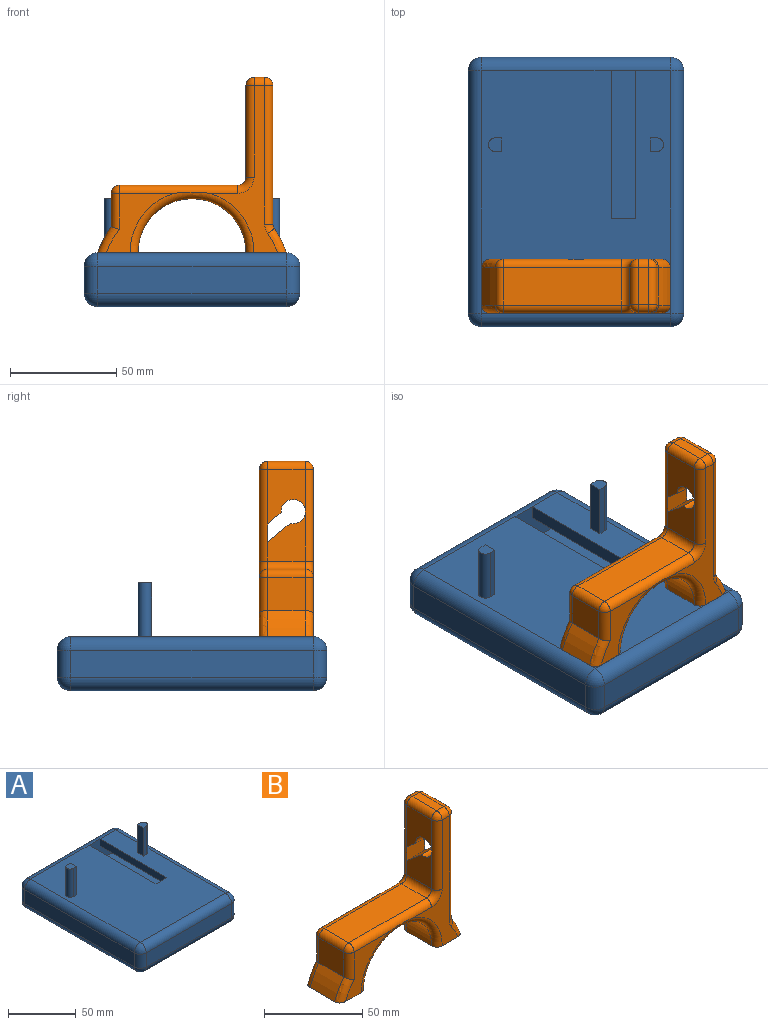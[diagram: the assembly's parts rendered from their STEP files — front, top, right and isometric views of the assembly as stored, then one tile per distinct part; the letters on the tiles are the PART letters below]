
ASSEMBLY  parts=2 mates=1
PART A: 45 faces, bbox 101.6x127x50.8 mm
  f0: plane 114.3x88.9mm, normal (0,0,1), area 9290.9mm2, adj f9,f10,f19,f20,f26,f27,f28,f29
  f1: plane 114.3x12.7mm, normal (-1,0,0), area 1451.6mm2, adj f14,f19,f22,f25
  f2: plane 88.9x12.7mm, normal (0,-1,0), area 1129mm2, adj f11,f20,f21,f25
  f3: plane 114.3x12.7mm, normal (1,0,0), area 1451.6mm2, adj f6,f10,f11,f12
  f4: plane 88.9x12.7mm, normal (0,1,0), area 1129mm2, adj f6,f9,f13,f14
  f5: plane 114.3x88.9mm, normal (0,0,-1), area 10161.3mm2, adj f12,f13,f21,f22
  f6: cylinder r=6.35mm len=12.7mm, axis (0,0,1), area 126.7mm2, adj f3,f4,f7,f8
  f7: sphere r=6.35mm, area 63.3mm2, adj f6,f9,f10
  f8: sphere r=6.35mm, area 63.3mm2, adj f6,f12,f13
  f9: cylinder r=6.35mm len=88.9mm, axis (1,0,0), area 886.7mm2, adj f0,f4,f7,f15,f42
  f10: cylinder r=6.35mm len=114.3mm, axis (0,-1,0), area 1140.1mm2, adj f0,f3,f7,f16
  f11: cylinder r=6.35mm len=12.7mm, axis (0,0,-1), area 126.7mm2, adj f2,f3,f16,f17
  f12: cylinder r=6.35mm len=114.3mm, axis (0,1,0), area 1140.1mm2, adj f3,f5,f8,f17
  f13: cylinder r=6.35mm len=88.9mm, axis (-1,0,0), area 886.7mm2, adj f4,f5,f8,f18
  f14: cylinder r=6.35mm len=12.7mm, axis (0,0,-1), area 126.7mm2, adj f1,f4,f15,f18
  f15: sphere r=6.35mm, area 63.3mm2, adj f9,f14,f19
  f16: sphere r=6.35mm, area 63.3mm2, adj f10,f11,f20
  f17: sphere r=6.35mm, area 63.3mm2, adj f11,f12,f21
  f18: sphere r=6.35mm, area 63.3mm2, adj f13,f14,f22
  f19: cylinder r=6.35mm len=114.3mm, axis (0,1,0), area 1140.1mm2, adj f0,f1,f15,f23
  f20: cylinder r=6.35mm len=88.9mm, axis (-1,0,0), area 886.7mm2, adj f0,f2,f16,f23
  f21: cylinder r=6.35mm len=88.9mm, axis (1,0,0), area 886.7mm2, adj f2,f5,f17,f24
  f22: cylinder r=6.35mm len=114.3mm, axis (0,-1,0), area 1140.1mm2, adj f1,f5,f18,f24
  f23: sphere r=6.35mm, area 63.3mm2, adj f19,f20,f25
  f24: sphere r=6.35mm, area 63.3mm2, adj f21,f22,f25
  f25: cylinder r=6.35mm len=12.7mm, axis (0,0,1), area 126.7mm2, adj f1,f2,f23,f24
  f26: plane 25.4x3.18mm, normal (0,-1,0), area 80.6mm2, adj f0,f27,f29,f30
  f27: plane 25.4x6.35mm, normal (1,0,0), area 161.3mm2, adj f0,f26,f28,f30
  f28: plane 25.4x3.18mm, normal (0,1,0), area 80.6mm2, adj f0,f27,f29,f30
  f29: cylinder r=3.17mm len=25.4mm, axis (0,0,-1), area 253.4mm2, adj f0,f26,f28,f30
  f30: plane 6.35x6.35mm, normal (0,0,1), area 36mm2, adj f26,f27,f28,f29
  f31: plane 25.4x6.35mm, normal (-1,0,0), area 161.3mm2, adj f0,f32,f34,f35
  f32: plane 25.4x3.18mm, normal (0,-1,0), area 80.6mm2, adj f0,f31,f33,f35
  f33: cylinder r=3.17mm len=25.4mm, axis (0,0,-1), area 253.4mm2, adj f0,f32,f34,f35
  f34: plane 25.4x3.18mm, normal (0,1,0), area 80.6mm2, adj f0,f31,f33,f35
  f35: plane 6.35x6.35mm, normal (0,0,1), area 36mm2, adj f31,f32,f33,f34
  f36: plane 11.43x6.35mm, normal (0,1,0), area 72.6mm2, adj f0,f37,f38,f43
  f37: plane 69.85x6.35mm, normal (-1,0,0), area 443.5mm2, adj f0,f36,f42,f43
  f38: plane 69.85x6.35mm, normal (1,0,0), area 443.5mm2, adj f0,f36,f42,f43
  f39: plane 114.3x12.7mm, normal (1,0,0), area 1451.6mm2, adj f40,f42,f43,f44
  f40: plane 88.9x12.7mm, normal (0,1,0), area 1129mm2, adj f39,f41,f43,f44
  f41: plane 114.3x12.7mm, normal (-1,0,0), area 1451.6mm2, adj f40,f42,f43,f44
  f42: plane 88.9x19.05mm, normal (0,-1,0), area 1201.6mm2, adj f9,f37,f38,f39,f41,f43,f44
  f43: plane 114.3x88.9mm, normal (0,0,-1), area 9362.9mm2, adj f36,f37,f38,f39,f40,f41,f42
  f44: plane 114.3x88.9mm, normal (0,0,1), area 10161.3mm2, adj f39,f40,f41,f42
PART B: 53 faces, bbox 89.9x25.4x84.7 mm
  f0: plane 25.67x17.78mm, normal (1,0,0), area 321.6mm2, adj f19,f29,f30,f51,f52
  f1: plane 25.67x17.78mm, normal (-1,0,0), area 321.6mm2, adj f34,f40,f46,f51,f52
  f2: plane 31.88x27.94mm, normal (0,1,0), area 332.7mm2, adj f6,f18,f22,f27,f33
  f3: plane 31.88x27.94mm, normal (0,-1,0), area 332.7mm2, adj f6,f25,f31,f37,f42
  f4: plane 17.78x15.68mm, normal (-1,0,0), area 278.7mm2, adj f5,f22,f31,f32
  f5: cylinder r=46.99mm len=17.78mm, axis (0,1,0), area 246.4mm2, adj f4,f6,f18,f25
  f6: plane 25.4x19.05mm, normal (0,0,-1), area 471mm2, adj f2,f3,f5,f7,f18,f25,f27,f37
  f7: cylinder r=25.4mm len=50.8mm, axis (0,1,0), area 1418.8mm2, adj f6,f8,f27,f37
  f8: plane 25.4x19.05mm, normal (0,0,-1), area 471mm2, adj f7,f9,f14,f15,f16,f21,f27,f37
  f9: cylinder r=46.99mm len=17.78mm, axis (0,1,0), area 225.8mm2, adj f8,f16,f20,f21
  f10: plane 44.96x17.78mm, normal (1,0,0), area 667.7mm2, adj f19,f20,f30,f48,f49
  f11: plane 17.78x5.08mm, normal (0,0,1), area 90.3mm2, adj f28,f29,f40,f41
  f12: plane 22.87x17.78mm, normal (-1,0,0), area 274.9mm2, adj f34,f43,f46,f48,f49
  f13: plane 55.88x17.78mm, normal (0,0,1), area 993.5mm2, adj f32,f33,f42,f43
  f14: plane 78.74x31.88mm, normal (0,-1,0), area 603.8mm2, adj f8,f21,f24,f30,f37,f41,f42,f45
  f15: plane 78.74x31.88mm, normal (0,1,0), area 603.8mm2, adj f8,f16,f17,f19,f27,f28,f33,f34
  f16: torus R=43.18mm, axis (0,-1,0), area 70.9mm2, adj f8,f9,f15,f17
  f17: torus R=7.62mm, axis (0,-1,0), area 18.7mm2, adj f15,f16,f19,f20
  f18: torus R=43.18mm, axis (0,-1,0), area 80.3mm2, adj f2,f5,f6,f22
  f19: cylinder r=3.81mm len=65.27mm, axis (0,0,1), area 390.6mm2, adj f0,f10,f15,f17,f23,f50
  f20: cylinder r=3.81mm len=17.78mm, axis (0,1,0), area 40.7mm2, adj f9,f10,f17,f24
  f21: torus R=43.18mm, axis (0,-1,0), area 70.9mm2, adj f8,f9,f14,f24
  f22: cylinder r=3.81mm len=16.94mm, axis (0,0,-1), area 96.5mm2, adj f2,f4,f18,f26
  f23: sphere r=3.81mm, area 22.8mm2, adj f19,f28,f29
  f24: torus R=7.62mm, axis (0,-1,0), area 18.7mm2, adj f14,f20,f21,f30
  f25: torus R=43.18mm, axis (0,-1,0), area 80.3mm2, adj f3,f5,f6,f31
  f26: sphere r=3.81mm, area 22.8mm2, adj f22,f32,f33
  f27: torus R=29.21mm, axis (0,-1,0), area 496.3mm2, adj f2,f6,f7,f8,f15,f33
  f28: cylinder r=3.81mm len=5.08mm, axis (-1,0,0), area 30.4mm2, adj f11,f15,f23,f35
  f29: cylinder r=3.81mm len=17.78mm, axis (0,-1,0), area 106.4mm2, adj f0,f11,f23,f36
  f30: cylinder r=3.81mm len=65.27mm, axis (0,0,-1), area 390.6mm2, adj f0,f10,f14,f24,f36,f47
  f31: cylinder r=3.81mm len=16.94mm, axis (0,0,1), area 96.5mm2, adj f3,f4,f25,f38
  f32: cylinder r=3.81mm len=17.78mm, axis (0,-1,0), area 106.4mm2, adj f4,f13,f26,f38
  f33: cylinder r=3.81mm len=55.88mm, axis (-1,0,0), area 327.2mm2, adj f2,f13,f15,f26,f27,f39
  f34: cylinder r=3.81mm len=43.18mm, axis (0,0,-1), area 258.4mm2, adj f1,f12,f15,f35,f39,f50
  f35: sphere r=3.81mm, area 22.8mm2, adj f28,f34,f40
  f36: sphere r=3.81mm, area 22.8mm2, adj f29,f30,f41
  f37: torus R=29.21mm, axis (0,-1,0), area 496.3mm2, adj f3,f6,f7,f8,f14,f42
  f38: sphere r=3.81mm, area 22.8mm2, adj f31,f32,f42
  f39: torus R=7.62mm, axis (0,-1,0), area 48.8mm2, adj f15,f33,f34,f43
  f40: cylinder r=3.81mm len=17.78mm, axis (0,1,0), area 106.4mm2, adj f1,f11,f35,f44
  f41: cylinder r=3.81mm len=5.08mm, axis (1,0,0), area 30.4mm2, adj f11,f14,f36,f44
  f42: cylinder r=3.81mm len=55.88mm, axis (1,0,0), area 327.2mm2, adj f3,f13,f14,f37,f38,f45
  f43: cylinder r=3.81mm len=17.78mm, axis (0,1,0), area 106.4mm2, adj f12,f13,f39,f45
  f44: sphere r=3.81mm, area 22.8mm2, adj f40,f41,f46
  f45: torus R=7.62mm, axis (0,-1,0), area 48.8mm2, adj f14,f42,f43,f46
  f46: cylinder r=3.81mm len=43.18mm, axis (0,0,1), area 258.4mm2, adj f1,f12,f14,f44,f45,f47
  f47: plane 12.7x0.94mm, normal (0,1,0), area 11.9mm2, adj f30,f46,f48,f52
  f48: cylinder r=5.71mm len=12.7mm, axis (1,0,0), area 126.7mm2, adj f10,f12,f47,f49
  f49: plane 12.7x10.63mm, normal (0,0.64,0.77), area 176.3mm2, adj f10,f12,f48,f50
  f50: plane 12.7x8.62mm, normal (0,-1,0), area 109.5mm2, adj f19,f34,f49,f51
  f51: plane 12.7x6.39mm, normal (0,-0.64,-0.77), area 105.9mm2, adj f0,f1,f50,f52
  f52: cylinder r=5.71mm len=12.7mm, axis (1,0,0), area 228mm2, adj f0,f1,f47,f51
PLACE A t=(-2.29,-6.69,-25.04)mm fixed
PLACE B t=(-2.28,-38.44,0.36)mm
MATE fastened A.f25 <-> B.f6  axis (0,0,1) through (-46.74,-63.84,0.36)mm
